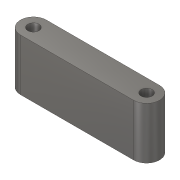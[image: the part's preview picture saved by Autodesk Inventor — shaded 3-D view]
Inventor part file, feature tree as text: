
AUTODESK INVENTOR PART (.ipt)
format: ipt  version: 2019.4 (Build 234330000, 330)  size: 92,672 bytes
history: native  units: in
note: dims shown in document units (in); Inventor stores cm internally (conversion verified against a paired STEP export)
features: extrude x1, sketch x1
ambient origin geometry x8: Origin, YZ Plane, XZ Plane, XY Plane, X Axis, Y Axis, Z Axis, Center Point
bodies: Solid1 (feature_tree)
feature tree (2):
  extrude  "Extrusion1"  Depth=1.0in
  sketch  "Sketch1"  dims[d0=0.2188in d1=2.1875in d2=0.25in d3=1.0in d4=0.0in]
